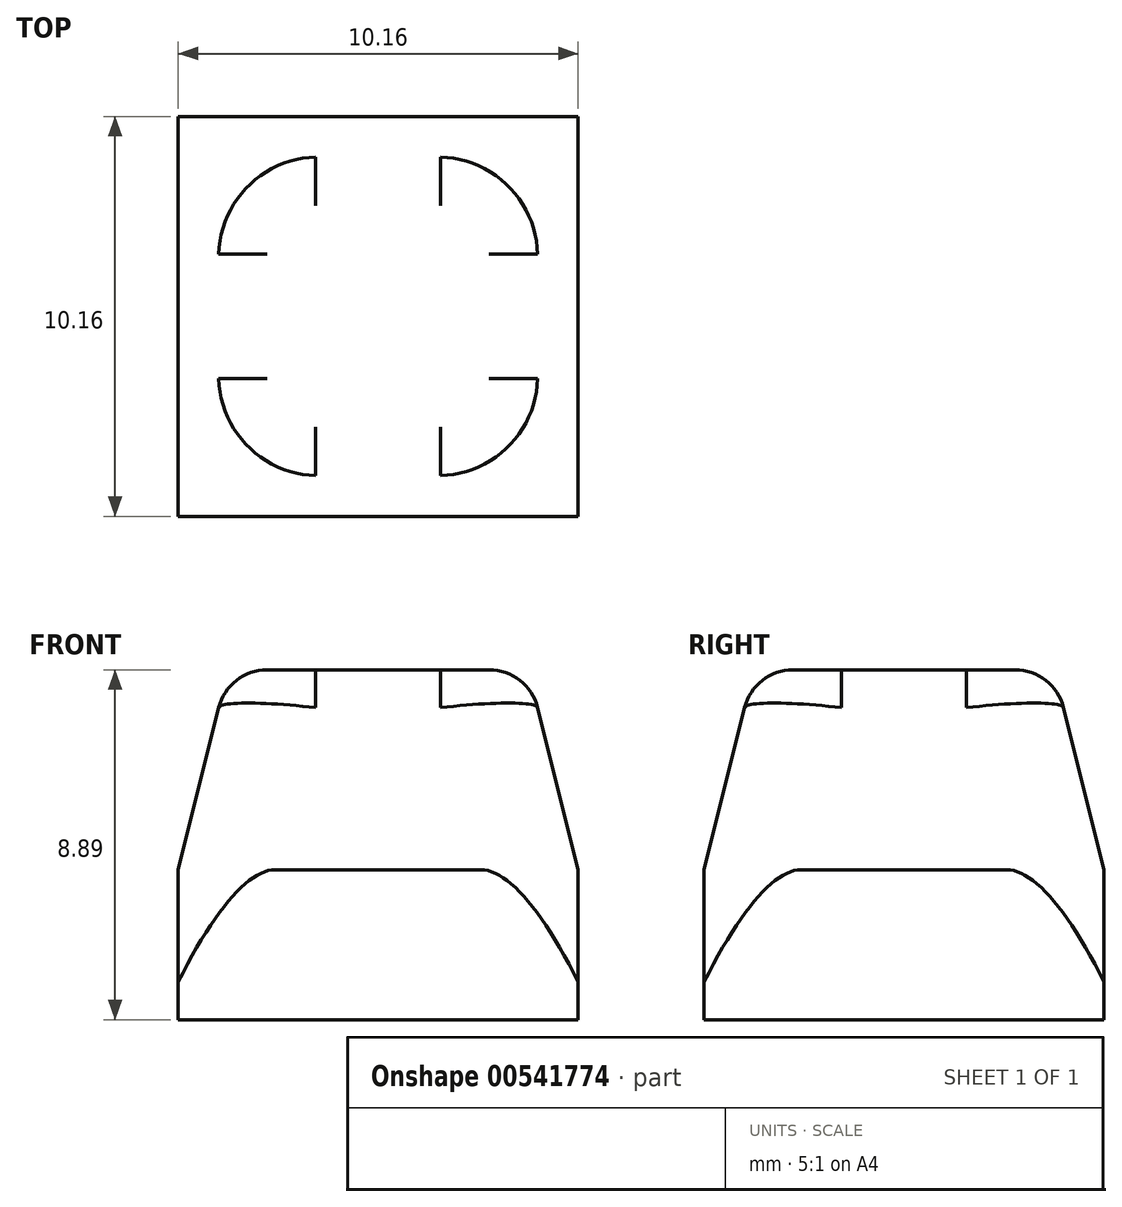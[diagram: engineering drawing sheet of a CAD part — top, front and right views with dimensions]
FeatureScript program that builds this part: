
annotation { "Feature Type Name" : "Feature", "Feature Type Description" : "" }
export const myFeature = defineFeature(function(context is Context, id is Id, definition is map)
    precondition{}
    {
        {
            var Q0;
            Q0=qCreatedBy(makeId("Top.planeOp"),FACE);
            var sketch = newSketch(context, id + "F0", { "sketchPlane" : qUnion([Q0])});
            skLineSegment(sketch, "E0.bottom", {"start": v(0, 0) * mm, "end": v(10.16, 0) * mm});
            skLineSegment(sketch, "E0.top", {"start": v(0, 10.16) * mm, "end": v(10.16, 10.16) * mm});
            skLineSegment(sketch, "E0.left", {"start": v(0, 0) * mm, "end": v(0, 10.16) * mm});
            skLineSegment(sketch, "E0.right", {"start": v(10.16, 0) * mm, "end": v(10.16, 10.16) * mm});
            skSolve(sketch);
        }
        {
            var Q0;
            Q0=makeQuery(id+"F0.imprint","IMPRINT",FACE,{"disambiguationData":[TD([[makeQuery(id+"F0.imprint","IMPRINT",EDGE,{"derivedFrom":sQuery(id+"F0.wireOp",EDGE,"E0.bottom")}),1.0]])]});
            extrude(context, id + "F1", {"entities" : qUnion([Q0]), "depth" : 8.9 * mm, "offsetDistance" : 25.4 * mm});
        }
        {
            var Q0;
            Q0=makeQuery(id+"F1.opExtrude","CAP_EDGE",EDGE,{"disambiguationData":[OSD([sQuery(id+"F0.wireOp",EDGE,"E0.right")])],"isStart":false});
            var Q1;
            Q1=makeQuery(id+"F1.opExtrude","CAP_EDGE",EDGE,{"disambiguationData":[OSD([sQuery(id+"F0.wireOp",EDGE,"E0.bottom")])],"isStart":false});
            var Q2;
            Q2=makeQuery(id+"F1.opExtrude","CAP_EDGE",EDGE,{"disambiguationData":[OSD([sQuery(id+"F0.wireOp",EDGE,"E0.left")])],"isStart":false});
            var Q3;
            Q3=makeQuery(id+"F1.opExtrude","CAP_EDGE",EDGE,{"disambiguationData":[OSD([sQuery(id+"F0.wireOp",EDGE,"E0.top")])],"isStart":false});
            chamfer(context, id + "F2", {"entities" : qUnion([Q0, Q1, Q2, Q3]), "chamferType" : ChamferType.TWO_OFFSETS, "width1" : 1.27 * mm, "oppositeDirection" : false, "width2" : 5.08 * mm, "tangentPropagation" : true});
        }
        {
            var Q0;
            Q0=makeQuery(id+"F2.opChamfer","BLEND_EDGE",EDGE,{"blendedFrom":[makeQuery(id+"F1.opExtrude","CAP_EDGE",EDGE,{"disambiguationData":[OSD([sQuery(id+"F0.wireOp",EDGE,"E0.bottom")])],"isStart":false}),makeQuery(id+"F1.opExtrude","CAP_EDGE",EDGE,{"disambiguationData":[OSD([sQuery(id+"F0.wireOp",EDGE,"E0.right")])],"isStart":false})],"blendedInto":[]});
            var Q1;
            Q1=makeQuery(id+"F2.opChamfer","BLEND_EDGE",EDGE,{"blendedFrom":[makeQuery(id+"F1.opExtrude","CAP_EDGE",EDGE,{"disambiguationData":[OSD([sQuery(id+"F0.wireOp",EDGE,"E0.top")])],"isStart":false}),makeQuery(id+"F1.opExtrude","CAP_EDGE",EDGE,{"disambiguationData":[OSD([sQuery(id+"F0.wireOp",EDGE,"E0.right")])],"isStart":false})],"blendedInto":[]});
            var Q2;
            Q2=makeQuery(id+"F2.opChamfer","BLEND_EDGE",EDGE,{"blendedFrom":[makeQuery(id+"F1.opExtrude","CAP_EDGE",EDGE,{"disambiguationData":[OSD([sQuery(id+"F0.wireOp",EDGE,"E0.top")])],"isStart":false}),makeQuery(id+"F1.opExtrude","CAP_EDGE",EDGE,{"disambiguationData":[OSD([sQuery(id+"F0.wireOp",EDGE,"E0.left")])],"isStart":false})],"blendedInto":[]});
            var Q3;
            Q3=makeQuery(id+"F2.opChamfer","BLEND_EDGE",EDGE,{"blendedFrom":[makeQuery(id+"F1.opExtrude","CAP_EDGE",EDGE,{"disambiguationData":[OSD([sQuery(id+"F0.wireOp",EDGE,"E0.bottom")])],"isStart":false}),makeQuery(id+"F1.opExtrude","CAP_EDGE",EDGE,{"disambiguationData":[OSD([sQuery(id+"F0.wireOp",EDGE,"E0.left")])],"isStart":false})],"blendedInto":[]});
            fillet(context, id + "F3", {"entities" : qUnion([Q0, Q1, Q2, Q3]), "radius" : 2.54 * mm, "tangentPropagation" : true, "allowEdgeOverflow" : false});
        }
        {
            var Q0;
            {var subQ0=sQuery(id+"F0.wireOp",EDGE,"E0.left");var subQ1=sQuery(id+"F0.wireOp",EDGE,"E0.top");Q0=makeQuery(id+"F3.opFillet","BLEND_EDGE",EDGE,{"blendedFrom":[makeQuery(id+"F2.opChamfer","BLEND_EDGE",EDGE,{"blendedFrom":[makeQuery(id+"F1.opExtrude","CAP_EDGE",EDGE,{"disambiguationData":[OSD([subQ1])],"isStart":false}),makeQuery(id+"F1.opExtrude","CAP_EDGE",EDGE,{"disambiguationData":[OSD([subQ0])],"isStart":false})],"blendedInto":[]}),makeQuery(id+"F1.opExtrude","CAP_FACE",FACE,{"disambiguationData":[OSD([sQuery(id+"F0.wireOp",EDGE,"E0.bottom"),subQ1,subQ0,sQuery(id+"F0.wireOp",EDGE,"E0.right")])],"isStart":false})],"blendedInto":[makeQuery(id+"F1.opExtrude","CAP_FACE",FACE,{"disambiguationData":[OSD([sQuery(id+"F0.wireOp",EDGE,"E0.bottom"),subQ1,subQ0,sQuery(id+"F0.wireOp",EDGE,"E0.right")])],"isStart":false})]});}
            fillet(context, id + "F4", {"entities" : qUnion([Q0]), "radius" : 1.27 * mm, "tangentPropagation" : true, "allowEdgeOverflow" : false});
        }
    });
